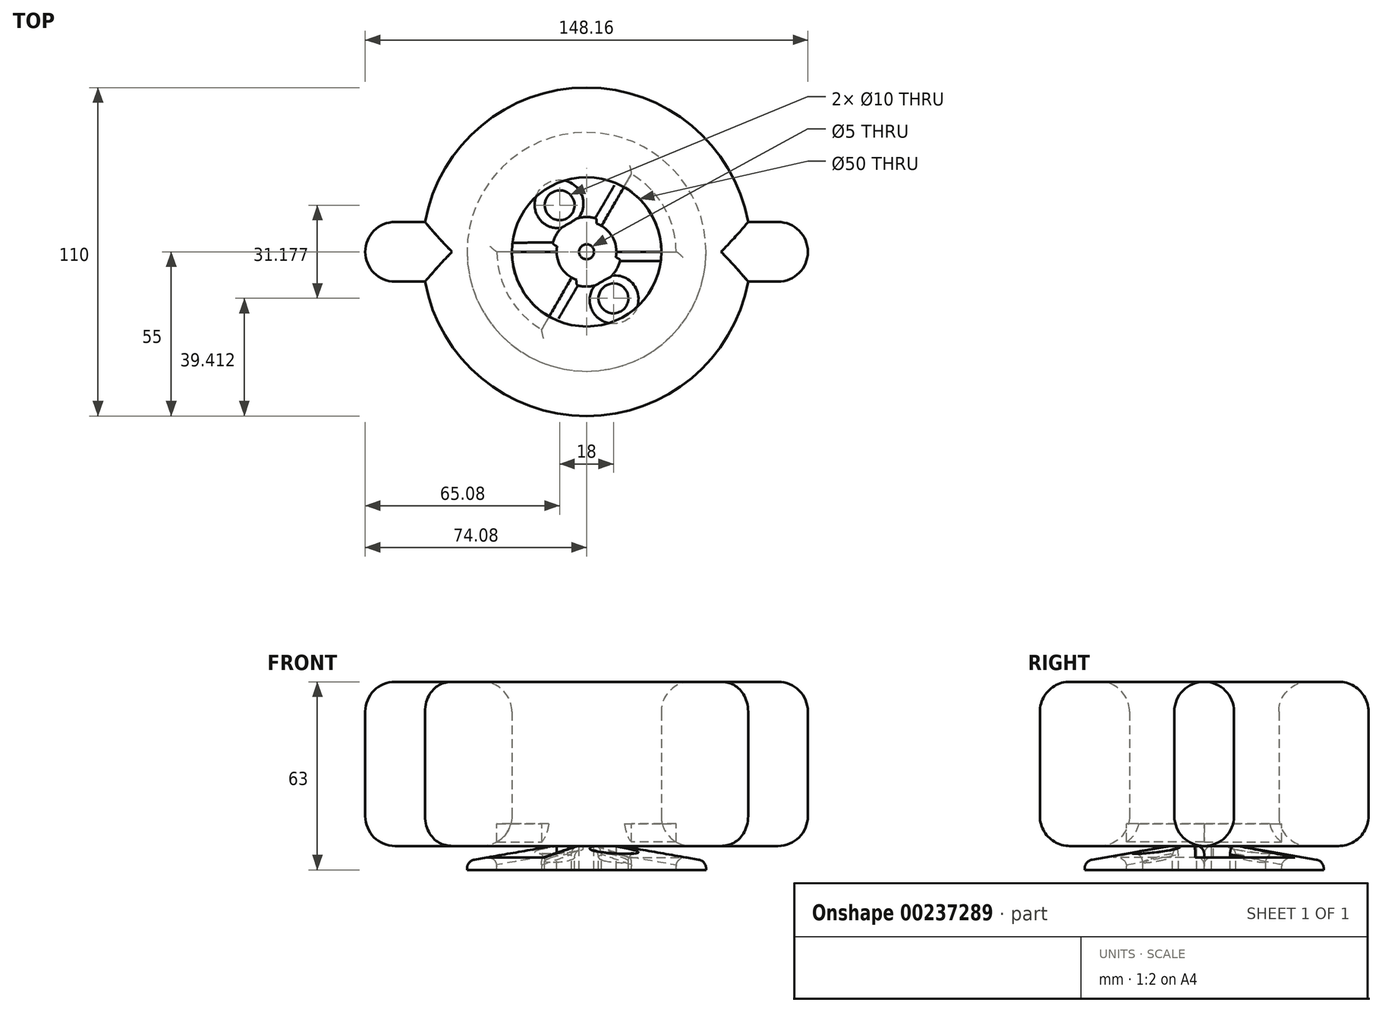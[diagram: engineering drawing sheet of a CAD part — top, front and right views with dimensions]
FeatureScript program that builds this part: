
annotation { "Feature Type Name" : "Feature", "Feature Type Description" : "" }
export const myFeature = defineFeature(function(context is Context, id is Id, definition is map)
    precondition{}
    {
        {
            var Q0;
            Q0=qCreatedBy(makeId("Top.planeOp"),FACE);
            var sketch = newSketch(context, id + "F0", { "sketchPlane" : qUnion([Q0])});
            skCircle(sketch, "E0", {"center": v(0, 0) * mm, "radius": 55 * mm});
            skCircle(sketch, "E1", {"center": v(0, 0) * mm, "radius": 25 * mm});
            skLineSegment(sketch, "E2", {"start": v(-54.08, 10) * mm, "end": v(-74.08, 10) * mm});
            skLineSegment(sketch, "E3", {"start": v(-74.08, 10) * mm, "end": v(-74.08, -10) * mm});
            skLineSegment(sketch, "E4", {"start": v(-74.08, -10) * mm, "end": v(-54.08, -10) * mm});
            skLineSegment(sketch, "E5", {"start": v(54.08, 10) * mm, "end": v(74.08, 10) * mm});
            skLineSegment(sketch, "E6", {"start": v(74.08, 10) * mm, "end": v(74.08, -10) * mm});
            skLineSegment(sketch, "E7", {"start": v(74.08, -10) * mm, "end": v(54.08, -10) * mm});
            skSolve(sketch);
        }
        {
            var Q0;
            Q0=makeQuery(id+"F0.imprint","IMPRINT",FACE,{"disambiguationData":[TD([[makeQuery(id+"F0.imprint","IMPRINT",EDGE,{"derivedFrom":sQuery(id+"F0.wireOp",EDGE,"E1")}),-1.0]])]});
            var Q1;
            {var subQ0=sQuery(id+"F0.wireOp",EDGE,"E5");Q1=makeQuery(id+"F0.imprint","IMPRINT",FACE,{"disambiguationData":[TD([[makeQuery(id+"F0.imprint","IMPRINT",EDGE,{"derivedFrom":subQ0}),-1.0]])]});}
            var Q2;
            {var subQ0=sQuery(id+"F0.wireOp",EDGE,"E2");Q2=makeQuery(id+"F0.imprint","IMPRINT",FACE,{"disambiguationData":[TD([[makeQuery(id+"F0.imprint","IMPRINT",EDGE,{"derivedFrom":subQ0}),1.0]])]});}
            extrude(context, id + "F1", {"entities" : qUnion([Q0, Q1, Q2]), "depth" : 55 * mm, "offsetDistance" : 25 * mm});
        }
        {
            var Q0;
            Q0=makeQuery(id+"F1.opExtrude","CAP_FACE",FACE,{"disambiguationData":[OSD([sQuery(id+"F0.wireOp",EDGE,"E0"),sQuery(id+"F0.wireOp",EDGE,"E1"),sQuery(id+"F0.wireOp",EDGE,"E2"),sQuery(id+"F0.wireOp",EDGE,"E3"),sQuery(id+"F0.wireOp",EDGE,"E4"),sQuery(id+"F0.wireOp",EDGE,"E5"),sQuery(id+"F0.wireOp",EDGE,"E6"),sQuery(id+"F0.wireOp",EDGE,"E7")])],"isStart":false});
            var Q1;
            Q1=makeQuery(id+"F1.opExtrude","CAP_FACE",FACE,{"disambiguationData":[OSD([sQuery(id+"F0.wireOp",EDGE,"E0"),sQuery(id+"F0.wireOp",EDGE,"E1"),sQuery(id+"F0.wireOp",EDGE,"E2"),sQuery(id+"F0.wireOp",EDGE,"E3"),sQuery(id+"F0.wireOp",EDGE,"E4"),sQuery(id+"F0.wireOp",EDGE,"E5"),sQuery(id+"F0.wireOp",EDGE,"E6"),sQuery(id+"F0.wireOp",EDGE,"E7")])],"isStart":true});
            var Q2;
            Q2=makeQuery(id+"F1.opExtrude","SWEPT_FACE",FACE,{"disambiguationData":[OSD([sQuery(id+"F0.wireOp",EDGE,"E3")])]});
            var Q3;
            Q3=makeQuery(id+"F1.opExtrude","SWEPT_FACE",FACE,{"disambiguationData":[OSD([sQuery(id+"F0.wireOp",EDGE,"E6")])]});
            fillet(context, id + "F2", {"entities" : qUnion([Q0, Q1, Q2, Q3]), "radius" : 10 * mm, "tangentPropagation" : true, "allowEdgeOverflow" : false});
        }
        {
            var Q0;
            Q0=qCreatedBy(makeId("Top.planeOp"),FACE);
            cPlane(context, id + "F3", {"entities" : qUnion([Q0]), "cplaneType" : CPlaneType.OFFSET, "offset" : 5 * mm, "oppositeDirection" : true, "width" : 150 * mm, "height" : 150 * mm});
        }
        {
            var Q0;
            Q0=qCreatedBy(id+"F3.planeOp",FACE);
            var sketch = newSketch(context, id + "F4", { "sketchPlane" : qUnion([Q0])});
            skCircle(sketch, "E8", {"center": v(0, 0) * mm, "radius": 40 * mm});
            skCircle(sketch, "E9", {"center": v(0, 0) * mm, "radius": 30 * mm});
            skCircle(sketch, "E10", {"center": v(0, 0) * mm, "radius": 10 * mm});
            skCircle(sketch, "E11", {"center": v(0, 0) * mm, "radius": 2.5 * mm});
            skLineSegment(sketch, "E12", {"start": v(10, 0) * mm, "end": v(30, 0) * mm});
            skLineSegment(sketch, "E13", {"start": v(0, 0) * mm, "end": v(15, 25.98) * mm});
            skLineSegment(sketch, "E14", {"start": v(0, 0) * mm, "end": v(-15, -25.98) * mm});
            skLineSegment(sketch, "E15", {"start": v(10, 0) * mm, "end": v(-30, 0) * mm});
            skCircle(sketch, "E16", {"center": v(9, -15.59) * mm, "radius": 5 * mm});
            skLineSegment(sketch, "E17", {"start": v(-15, -25.98) * mm, "end": v(30, 0) * mm, "construction": true});
            skLineSegment(sketch, "E18", {"start": v(-11.78, -27.59) * mm, "end": v(29.78, -3.59) * mm, "construction": true});
            skCircle(sketch, "E19.1.0", {"center": v(-9, 15.59) * mm, "radius": 5 * mm});
            skSolve(sketch);
        }
        {
            var Q0;
            {var subQ3=sQuery(id+"F4.wireOp",EDGE,"3556ffb3-3399-4bb4-9b4c-37cd51f6e398.1.0");Q0=makeQuery(id+"F4.imprint","IMPRINT",FACE,{"disambiguationData":[TD([[makeQuery(id+"F4.imprint","IMPRINT",EDGE,{"derivedFrom":subQ3}),-1.0]])]});}
            var Q1;
            {var subQ3=sQuery(id+"F4.wireOp",EDGE,"3556ffb3-3399-4bb4-9b4c-37cd51f6e398.2.0");Q1=makeQuery(id+"F4.imprint","IMPRINT",FACE,{"disambiguationData":[TD([[makeQuery(id+"F4.imprint","IMPRINT",EDGE,{"derivedFrom":subQ3}),-1.0]])]});}
            var Q2;
            {var subQ3=sQuery(id+"F4.wireOp",EDGE,"3556ffb3-3399-4bb4-9b4c-37cd51f6e398.3.0");Q2=makeQuery(id+"F4.imprint","IMPRINT",FACE,{"disambiguationData":[TD([[makeQuery(id+"F4.imprint","IMPRINT",EDGE,{"derivedFrom":subQ3}),-1.0]])]});}
            var Q3;
            {var subQ0=sQuery(id+"F4.wireOp",EDGE,"E12");Q3=makeQuery(id+"F4.imprint","IMPRINT",FACE,{"disambiguationData":[TD([[makeQuery(id+"F4.imprint","IMPRINT",EDGE,{"derivedFrom":subQ0}),-1.0]])]});}
            var Q4;
            Q4=makeQuery(id+"F4.imprint","IMPRINT",FACE,{"disambiguationData":[TD([[makeQuery(id+"F4.imprint","IMPRINT",EDGE,{"derivedFrom":sQuery(id+"F4.wireOp",EDGE,"E8")}),1.0]])]});
            var Q5;
            {var subQ1=sQuery(id+"F4.wireOp",EDGE,"E10");var subQ7=makeQuery(id+"F4.imprint","INTERSECT",VERTEX,{"derivedFrom":[subQ1,sQuery(id+"F4.wireOp",EDGE,"E12")]});Q5=makeQuery(id+"F4.imprint","IMPRINT",FACE,{"disambiguationData":[TD([[makeQuery(id+"F4.imprint","IMPRINT",EDGE,{"disambiguationData":[TD([[subQ7,-1.0]])],"derivedFrom":subQ1}),1.0]])]});}
            var Q6;
            {var subQ1=sQuery(id+"F4.wireOp",EDGE,"E10");var subQ5=makeQuery(id+"F4.imprint","INTERSECT",VERTEX,{"derivedFrom":[subQ1,sQuery(id+"F4.wireOp",EDGE,"3556ffb3-3399-4bb4-9b4c-37cd51f6e398.3.0")]});Q6=makeQuery(id+"F4.imprint","IMPRINT",FACE,{"disambiguationData":[TD([[makeQuery(id+"F4.imprint","IMPRINT",EDGE,{"disambiguationData":[TD([[subQ5,1.0]])],"derivedFrom":subQ1}),1.0]])]});}
            var Q7;
            {var subQ5=sQuery(id+"F4.wireOp",EDGE,"E10");var subQ6=makeQuery(id+"F4.imprint","INTERSECT",VERTEX,{"derivedFrom":[subQ5,sQuery(id+"F4.wireOp",EDGE,"3556ffb3-3399-4bb4-9b4c-37cd51f6e398.2.0")]});Q7=makeQuery(id+"F4.imprint","IMPRINT",FACE,{"disambiguationData":[TD([[makeQuery(id+"F4.imprint","IMPRINT",EDGE,{"disambiguationData":[TD([[subQ6,1.0]])],"derivedFrom":subQ5}),1.0]])]});}
            var Q8;
            {var subQ1=sQuery(id+"F4.wireOp",EDGE,"E10");var subQ7=makeQuery(id+"F4.imprint","INTERSECT",VERTEX,{"derivedFrom":[subQ1,sQuery(id+"F4.wireOp",EDGE,"3556ffb3-3399-4bb4-9b4c-37cd51f6e398.1.0")]});Q8=makeQuery(id+"F4.imprint","IMPRINT",FACE,{"disambiguationData":[TD([[makeQuery(id+"F4.imprint","IMPRINT",EDGE,{"disambiguationData":[TD([[subQ7,1.0]])],"derivedFrom":subQ1}),1.0]])]});}
            var Q9;
            {var subQ0=sQuery(id+"F4.wireOp",EDGE,"3556ffb3-3399-4bb4-9b4c-37cd51f6e398.2.0");Q9=makeQuery(id+"F4.imprint","IMPRINT",FACE,{"disambiguationData":[TD([[makeQuery(id+"F4.imprint","IMPRINT",EDGE,{"derivedFrom":subQ0}),1.0]])]});}
            var Q10;
            {var subQ0=sQuery(id+"F4.wireOp",EDGE,"E12");Q10=makeQuery(id+"F4.imprint","IMPRINT",FACE,{"disambiguationData":[TD([[makeQuery(id+"F4.imprint","IMPRINT",EDGE,{"derivedFrom":subQ0}),1.0]])]});}
            var Q11;
            {var subQ0=sQuery(id+"F4.wireOp",EDGE,"3556ffb3-3399-4bb4-9b4c-37cd51f6e398.3.0");Q11=makeQuery(id+"F4.imprint","IMPRINT",FACE,{"disambiguationData":[TD([[makeQuery(id+"F4.imprint","IMPRINT",EDGE,{"derivedFrom":subQ0}),1.0]])]});}
            var Q12;
            {var subQ0=sQuery(id+"F4.wireOp",EDGE,"3556ffb3-3399-4bb4-9b4c-37cd51f6e398.1.0");Q12=makeQuery(id+"F4.imprint","IMPRINT",FACE,{"disambiguationData":[TD([[makeQuery(id+"F4.imprint","IMPRINT",EDGE,{"derivedFrom":subQ0}),1.0]])]});}
            var Q13;
            {var subQ0=sQuery(id+"F4.wireOp",EDGE,"E13");var subQ1=sQuery(id+"F4.wireOp",EDGE,"E9");var subQ2=makeQuery(id+"F4.imprint","INTERSECT",VERTEX,{"derivedFrom":[subQ1,subQ0]});Q13=makeQuery(id+"F4.imprint","IMPRINT",FACE,{"disambiguationData":[TD([[makeQuery(id+"F4.imprint","IMPRINT",EDGE,{"disambiguationData":[TD([[subQ2,-1.0]])],"derivedFrom":subQ1}),1.0]])]});}
            var Q14;
            {var subQ0=sQuery(id+"F4.wireOp",EDGE,"E14");var subQ1=sQuery(id+"F4.wireOp",EDGE,"E9");var subQ2=makeQuery(id+"F4.imprint","INTERSECT",VERTEX,{"derivedFrom":[subQ1,subQ0]});Q14=makeQuery(id+"F4.imprint","IMPRINT",FACE,{"disambiguationData":[TD([[makeQuery(id+"F4.imprint","IMPRINT",EDGE,{"disambiguationData":[TD([[subQ2,1.0]])],"derivedFrom":subQ1}),1.0]])]});}
            var Q15;
            {var subQ0=sQuery(id+"F4.wireOp",EDGE,"E15");var subQ5=sQuery(id+"F4.wireOp",EDGE,"E11");var subQ7=makeQuery(id+"F4.imprint","INTERSECT",VERTEX,{"disambiguationData":[OD(0.0)],"derivedFrom":[subQ5,subQ0]});Q15=makeQuery(id+"F4.imprint","IMPRINT",FACE,{"disambiguationData":[TD([[makeQuery(id+"F4.imprint","IMPRINT",EDGE,{"disambiguationData":[TD([[subQ7,1.0]])],"derivedFrom":subQ5}),-1.0]])]});}
            var Q16;
            {var subQ0=sQuery(id+"F4.wireOp",EDGE,"E15");var subQ1=sQuery(id+"F4.wireOp",EDGE,"E11");var subQ2=makeQuery(id+"F4.imprint","INTERSECT",VERTEX,{"disambiguationData":[OD(0.0)],"derivedFrom":[subQ1,subQ0]});Q16=makeQuery(id+"F4.imprint","IMPRINT",FACE,{"disambiguationData":[TD([[makeQuery(id+"F4.imprint","IMPRINT",EDGE,{"disambiguationData":[TD([[subQ2,1.0]])],"derivedFrom":subQ1}),1.0]])]});}
            var Q17;
            {var subQ0=sQuery(id+"F4.wireOp",EDGE,"E13");var subQ1=sQuery(id+"F4.wireOp",EDGE,"E11");var subQ2=makeQuery(id+"F4.imprint","INTERSECT",VERTEX,{"derivedFrom":[subQ1,subQ0]});Q17=makeQuery(id+"F4.imprint","IMPRINT",FACE,{"disambiguationData":[TD([[makeQuery(id+"F4.imprint","IMPRINT",EDGE,{"disambiguationData":[TD([[subQ2,-1.0]])],"derivedFrom":subQ1}),1.0]])]});}
            var Q18;
            {var subQ0=sQuery(id+"F4.wireOp",EDGE,"E13");var subQ1=sQuery(id+"F4.wireOp",EDGE,"E11");var subQ2=makeQuery(id+"F4.imprint","INTERSECT",VERTEX,{"derivedFrom":[subQ1,subQ0]});Q18=makeQuery(id+"F4.imprint","IMPRINT",FACE,{"disambiguationData":[TD([[makeQuery(id+"F4.imprint","IMPRINT",EDGE,{"disambiguationData":[TD([[subQ2,1.0]])],"derivedFrom":subQ1}),1.0]])]});}
            var Q19;
            {var subQ0=sQuery(id+"F4.wireOp",EDGE,"E15");var subQ1=sQuery(id+"F4.wireOp",EDGE,"E11");var subQ2=makeQuery(id+"F4.imprint","INTERSECT",VERTEX,{"disambiguationData":[OD(1.0)],"derivedFrom":[subQ1,subQ0]});Q19=makeQuery(id+"F4.imprint","IMPRINT",FACE,{"disambiguationData":[TD([[makeQuery(id+"F4.imprint","IMPRINT",EDGE,{"disambiguationData":[TD([[subQ2,-1.0]])],"derivedFrom":subQ1}),1.0]])]});}
            var Q20;
            Q20=makeQuery(id+"F4.imprint","IMPRINT",FACE,{"disambiguationData":[TD([[makeQuery(id+"F4.imprint","IMPRINT",EDGE,{"derivedFrom":sQuery(id+"F4.wireOp",EDGE,"E19.1.0")}),1.0]])]});
            var Q21;
            Q21=makeQuery(id+"F4.imprint","IMPRINT",FACE,{"disambiguationData":[TD([[makeQuery(id+"F4.imprint","IMPRINT",EDGE,{"derivedFrom":sQuery(id+"F4.wireOp",EDGE,"E16")}),1.0]])]});
            extrude(context, id + "F5", {"entities" : qUnion([Q0, Q1, Q2, Q3, Q4, Q5, Q6, Q7, Q8, Q9, Q10, Q11, Q12, Q13, Q14, Q15, Q16, Q17, Q18, Q19, Q20, Q21]), "oppositeDirection" : true, "depth" : 3 * mm, "offsetDistance" : 25 * mm});
        }
        {
            var Q0;
            {var subQ0=sQuery(id+"F4.wireOp",EDGE,"E13");var subQ1=sQuery(id+"F4.wireOp",EDGE,"E10");var subQ2=makeQuery(id+"F4.imprint","INTERSECT",VERTEX,{"derivedFrom":[subQ1,subQ0]});Q0=makeQuery(id+"F4.imprint","IMPRINT",FACE,{"disambiguationData":[TD([[makeQuery(id+"F4.imprint","IMPRINT",EDGE,{"disambiguationData":[TD([[subQ2,-1.0]])],"derivedFrom":subQ1}),1.0]])]});}
            var Q1;
            {var subQ0=sQuery(id+"F4.wireOp",EDGE,"E15");var subQ1=sQuery(id+"F4.wireOp",EDGE,"E10");var subQ2=makeQuery(id+"F4.imprint","INTERSECT",VERTEX,{"derivedFrom":[subQ1,subQ0]});Q1=makeQuery(id+"F4.imprint","IMPRINT",FACE,{"disambiguationData":[TD([[makeQuery(id+"F4.imprint","IMPRINT",EDGE,{"disambiguationData":[TD([[subQ2,-1.0]])],"derivedFrom":subQ1}),1.0]])]});}
            var Q2;
            Q2=makeQuery(id+"F4.imprint","IMPRINT",FACE,{"disambiguationData":[TD([[makeQuery(id+"F4.imprint","IMPRINT",EDGE,{"derivedFrom":sQuery(id+"F4.wireOp",EDGE,"E8")}),1.0]])]});
            var Q3;
            {var subQ0=sQuery(id+"F4.wireOp",EDGE,"E12");Q3=makeQuery(id+"F4.imprint","IMPRINT",FACE,{"disambiguationData":[TD([[makeQuery(id+"F4.imprint","IMPRINT",EDGE,{"derivedFrom":subQ0}),-1.0]])]});}
            var Q4;
            {var subQ0=sQuery(id+"F4.wireOp",EDGE,"E13");var subQ1=sQuery(id+"F4.wireOp",EDGE,"E11");var subQ2=makeQuery(id+"F4.imprint","INTERSECT",VERTEX,{"derivedFrom":[subQ1,subQ0]});Q4=makeQuery(id+"F4.imprint","IMPRINT",FACE,{"disambiguationData":[TD([[makeQuery(id+"F4.imprint","IMPRINT",EDGE,{"disambiguationData":[TD([[subQ2,1.0]])],"derivedFrom":subQ1}),1.0]])]});}
            var Q5;
            {var subQ0=sQuery(id+"F4.wireOp",EDGE,"E13");var subQ1=sQuery(id+"F4.wireOp",EDGE,"E11");var subQ2=makeQuery(id+"F4.imprint","INTERSECT",VERTEX,{"derivedFrom":[subQ1,subQ0]});Q5=makeQuery(id+"F4.imprint","IMPRINT",FACE,{"disambiguationData":[TD([[makeQuery(id+"F4.imprint","IMPRINT",EDGE,{"disambiguationData":[TD([[subQ2,-1.0]])],"derivedFrom":subQ1}),1.0]])]});}
            var Q6;
            {var subQ0=sQuery(id+"F4.wireOp",EDGE,"E15");var subQ1=sQuery(id+"F4.wireOp",EDGE,"E11");var subQ2=makeQuery(id+"F4.imprint","INTERSECT",VERTEX,{"disambiguationData":[OD(1.0)],"derivedFrom":[subQ1,subQ0]});Q6=makeQuery(id+"F4.imprint","IMPRINT",FACE,{"disambiguationData":[TD([[makeQuery(id+"F4.imprint","IMPRINT",EDGE,{"disambiguationData":[TD([[subQ2,-1.0]])],"derivedFrom":subQ1}),1.0]])]});}
            var Q7;
            {var subQ0=sQuery(id+"F4.wireOp",EDGE,"E15");var subQ1=sQuery(id+"F4.wireOp",EDGE,"E11");var subQ2=makeQuery(id+"F4.imprint","INTERSECT",VERTEX,{"disambiguationData":[OD(0.0)],"derivedFrom":[subQ1,subQ0]});Q7=makeQuery(id+"F4.imprint","IMPRINT",FACE,{"disambiguationData":[TD([[makeQuery(id+"F4.imprint","IMPRINT",EDGE,{"disambiguationData":[TD([[subQ2,1.0]])],"derivedFrom":subQ1}),1.0]])]});}
            var Q8;
            {var subQ0=sQuery(id+"F4.wireOp",EDGE,"E13");var subQ1=sQuery(id+"F4.wireOp",EDGE,"E9");var subQ2=makeQuery(id+"F4.imprint","INTERSECT",VERTEX,{"derivedFrom":[subQ1,subQ0]});Q8=makeQuery(id+"F4.imprint","IMPRINT",FACE,{"disambiguationData":[TD([[makeQuery(id+"F4.imprint","IMPRINT",EDGE,{"disambiguationData":[TD([[subQ2,-1.0]])],"derivedFrom":subQ1}),1.0]])]});}
            var Q9;
            {var subQ0=sQuery(id+"F4.wireOp",EDGE,"E15");var subQ5=sQuery(id+"F4.wireOp",EDGE,"E11");var subQ7=makeQuery(id+"F4.imprint","INTERSECT",VERTEX,{"disambiguationData":[OD(0.0)],"derivedFrom":[subQ5,subQ0]});Q9=makeQuery(id+"F4.imprint","IMPRINT",FACE,{"disambiguationData":[TD([[makeQuery(id+"F4.imprint","IMPRINT",EDGE,{"disambiguationData":[TD([[subQ7,1.0]])],"derivedFrom":subQ5}),-1.0]])]});}
            var Q10;
            {var subQ3=sQuery(id+"F4.wireOp",EDGE,"E13");var subQ5=sQuery(id+"F4.wireOp",EDGE,"E11");var subQ6=makeQuery(id+"F4.imprint","INTERSECT",VERTEX,{"derivedFrom":[subQ5,subQ3]});Q10=makeQuery(id+"F4.imprint","IMPRINT",FACE,{"disambiguationData":[TD([[makeQuery(id+"F4.imprint","IMPRINT",EDGE,{"disambiguationData":[TD([[subQ6,1.0]])],"derivedFrom":subQ5}),-1.0]])]});}
            var Q11;
            {var subQ0=sQuery(id+"F4.wireOp",EDGE,"E12");Q11=makeQuery(id+"F4.imprint","IMPRINT",FACE,{"disambiguationData":[TD([[makeQuery(id+"F4.imprint","IMPRINT",EDGE,{"derivedFrom":subQ0}),1.0]])]});}
            var Q12;
            {var subQ0=sQuery(id+"F4.wireOp",EDGE,"E14");var subQ1=sQuery(id+"F4.wireOp",EDGE,"E9");var subQ2=makeQuery(id+"F4.imprint","INTERSECT",VERTEX,{"derivedFrom":[subQ1,subQ0]});Q12=makeQuery(id+"F4.imprint","IMPRINT",FACE,{"disambiguationData":[TD([[makeQuery(id+"F4.imprint","IMPRINT",EDGE,{"disambiguationData":[TD([[subQ2,1.0]])],"derivedFrom":subQ1}),1.0]])]});}
            var Q13;
            Q13=makeQuery(id+"F4.imprint","IMPRINT",FACE,{"disambiguationData":[TD([[makeQuery(id+"F4.imprint","IMPRINT",EDGE,{"derivedFrom":sQuery(id+"F4.wireOp",EDGE,"E19.1.0")}),1.0]])]});
            var Q14;
            Q14=makeQuery(id+"F4.imprint","IMPRINT",FACE,{"disambiguationData":[TD([[makeQuery(id+"F4.imprint","IMPRINT",EDGE,{"derivedFrom":sQuery(id+"F4.wireOp",EDGE,"E16")}),1.0]])]});
            extrude(context, id + "F6", {"entities" : qUnion([Q0, Q1, Q2, Q3, Q4, Q5, Q6, Q7, Q8, Q9, Q10, Q11, Q12, Q13, Q14]), "operationType" : NewBodyOperationType.ADD, "depth" : 5 * mm, "offsetDistance" : 25 * mm, "hasDraft" : true, "draftAngle" : 80 * degree, "draftPullDirection" : true});
        }
        {
            var Q0;
            {var subQ0=sQuery(id+"F4.wireOp",EDGE,"E14");var subQ1=sQuery(id+"F4.wireOp",EDGE,"E9");var subQ2=makeQuery(id+"F4.imprint","INTERSECT",VERTEX,{"derivedFrom":[subQ1,subQ0]});Q0=makeQuery(id+"F4.imprint","IMPRINT",FACE,{"disambiguationData":[TD([[makeQuery(id+"F4.imprint","IMPRINT",EDGE,{"disambiguationData":[TD([[subQ2,1.0]])],"derivedFrom":subQ1}),1.0]])]});}
            var Q1;
            {var subQ0=sQuery(id+"F4.wireOp",EDGE,"E15");var subQ1=sQuery(id+"F4.wireOp",EDGE,"E11");var subQ2=makeQuery(id+"F4.imprint","INTERSECT",VERTEX,{"disambiguationData":[OD(0.0)],"derivedFrom":[subQ1,subQ0]});Q1=makeQuery(id+"F4.imprint","IMPRINT",FACE,{"disambiguationData":[TD([[makeQuery(id+"F4.imprint","IMPRINT",EDGE,{"disambiguationData":[TD([[subQ2,1.0]])],"derivedFrom":subQ1}),1.0]])]});}
            var Q2;
            {var subQ0=sQuery(id+"F4.wireOp",EDGE,"E13");var subQ1=sQuery(id+"F4.wireOp",EDGE,"E11");var subQ2=makeQuery(id+"F4.imprint","INTERSECT",VERTEX,{"derivedFrom":[subQ1,subQ0]});Q2=makeQuery(id+"F4.imprint","IMPRINT",FACE,{"disambiguationData":[TD([[makeQuery(id+"F4.imprint","IMPRINT",EDGE,{"disambiguationData":[TD([[subQ2,-1.0]])],"derivedFrom":subQ1}),1.0]])]});}
            var Q3;
            {var subQ0=sQuery(id+"F4.wireOp",EDGE,"E13");var subQ1=sQuery(id+"F4.wireOp",EDGE,"E11");var subQ2=makeQuery(id+"F4.imprint","INTERSECT",VERTEX,{"derivedFrom":[subQ1,subQ0]});Q3=makeQuery(id+"F4.imprint","IMPRINT",FACE,{"disambiguationData":[TD([[makeQuery(id+"F4.imprint","IMPRINT",EDGE,{"disambiguationData":[TD([[subQ2,1.0]])],"derivedFrom":subQ1}),1.0]])]});}
            var Q4;
            {var subQ0=sQuery(id+"F4.wireOp",EDGE,"E15");var subQ1=sQuery(id+"F4.wireOp",EDGE,"E11");var subQ2=makeQuery(id+"F4.imprint","INTERSECT",VERTEX,{"disambiguationData":[OD(1.0)],"derivedFrom":[subQ1,subQ0]});Q4=makeQuery(id+"F4.imprint","IMPRINT",FACE,{"disambiguationData":[TD([[makeQuery(id+"F4.imprint","IMPRINT",EDGE,{"disambiguationData":[TD([[subQ2,-1.0]])],"derivedFrom":subQ1}),1.0]])]});}
            var Q5;
            {var subQ0=sQuery(id+"F4.wireOp",EDGE,"E12");Q5=makeQuery(id+"F4.imprint","IMPRINT",FACE,{"disambiguationData":[TD([[makeQuery(id+"F4.imprint","IMPRINT",EDGE,{"derivedFrom":subQ0}),1.0]])]});}
            var Q6;
            Q6=makeQuery(id+"F4.imprint","IMPRINT",FACE,{"disambiguationData":[TD([[makeQuery(id+"F4.imprint","IMPRINT",EDGE,{"derivedFrom":sQuery(id+"F4.wireOp",EDGE,"E19.1.0")}),1.0]])]});
            var Q7;
            Q7=makeQuery(id+"F4.imprint","IMPRINT",FACE,{"disambiguationData":[TD([[makeQuery(id+"F4.imprint","IMPRINT",EDGE,{"derivedFrom":sQuery(id+"F4.wireOp",EDGE,"E16")}),1.0]])]});
            extrude(context, id + "F7", {"entities" : qUnion([Q0, Q1, Q2, Q3, Q4, Q5, Q6, Q7]), "operationType" : NewBodyOperationType.REMOVE, "oppositeDirection" : true, "depth" : 25 * mm, "offsetDistance" : 25 * mm, "symmetric" : true});
        }
        {
            var Q0;
            Q0=makeQuery(id+"F7.boolean.opBoolean","INTERSECT",EDGE,{"derivedFrom":[makeQuery(id+"F6.opExtrude","SWEPT_FACE",FACE,{"disambiguationData":[OSD([sQuery(id+"F4.wireOp",EDGE,"E8")])]}),makeQuery(id+"F7.opExtrude","SWEPT_FACE",FACE,{"disambiguationData":[OSD([sQuery(id+"F4.wireOp",EDGE,"E19.1.0")])]})]});
            var Q1;
            Q1=makeQuery(id+"F7.boolean.opBoolean","INTERSECT",EDGE,{"derivedFrom":[makeQuery(id+"F6.opExtrude","SWEPT_FACE",FACE,{"disambiguationData":[OSD([sQuery(id+"F4.wireOp",EDGE,"E8")])]}),makeQuery(id+"F7.opExtrude","SWEPT_FACE",FACE,{"disambiguationData":[OSD([sQuery(id+"F4.wireOp",EDGE,"E16")])]})]});
            var Q2;
            Q2=makeQuery(id+"F7.boolean.opBoolean","INTERSECT",EDGE,{"derivedFrom":[makeQuery(id+"F6.opExtrude","SWEPT_FACE",FACE,{"disambiguationData":[OSD([sQuery(id+"F4.wireOp",EDGE,"E8")])]}),makeQuery(id+"F7.opExtrude","SWEPT_FACE",FACE,{"disambiguationData":[OSD([sQuery(id+"F4.wireOp",EDGE,"E13")])]})]});
            var Q3;
            {var subQ0=sQuery(id+"F4.wireOp",EDGE,"E9");Q3=makeQuery(id+"F7.boolean.opBoolean","INTERSECT",EDGE,{"derivedFrom":[makeQuery(id+"F6.opExtrude","SWEPT_FACE",FACE,{"disambiguationData":[OSD([sQuery(id+"F4.wireOp",EDGE,"E8")])]}),makeQuery(id+"F7.opExtrude","SWEPT_FACE",FACE,{"disambiguationData":[OSD([subQ0]),TDD([makeQuery(id+"F4.imprint","IMPRINT",EDGE,{"disambiguationData":[TD([[makeQuery(id+"F4.imprint","INTERSECT",VERTEX,{"derivedFrom":[subQ0,sQuery(id+"F4.wireOp",EDGE,"E12")]}),-1.0]])],"derivedFrom":subQ0})])]})]});}
            var Q4;
            Q4=makeQuery(id+"F7.boolean.opBoolean","INTERSECT",EDGE,{"derivedFrom":[makeQuery(id+"F6.opExtrude","SWEPT_FACE",FACE,{"disambiguationData":[OSD([sQuery(id+"F4.wireOp",EDGE,"E8")])]}),makeQuery(id+"F7.opExtrude","SWEPT_FACE",FACE,{"disambiguationData":[OSD([sQuery(id+"F4.wireOp",EDGE,"E12")])]})]});
            var Q5;
            Q5=makeQuery(id+"F7.boolean.opBoolean","INTERSECT",EDGE,{"derivedFrom":[makeQuery(id+"F6.opExtrude","SWEPT_FACE",FACE,{"disambiguationData":[OSD([sQuery(id+"F4.wireOp",EDGE,"E8")])]}),makeQuery(id+"F7.opExtrude","SWEPT_FACE",FACE,{"disambiguationData":[OSD([sQuery(id+"F4.wireOp",EDGE,"E14")])]})]});
            var Q6;
            {var subQ0=sQuery(id+"F4.wireOp",EDGE,"E9");Q6=makeQuery(id+"F7.boolean.opBoolean","INTERSECT",EDGE,{"derivedFrom":[makeQuery(id+"F6.opExtrude","SWEPT_FACE",FACE,{"disambiguationData":[OSD([sQuery(id+"F4.wireOp",EDGE,"E8")])]}),makeQuery(id+"F7.opExtrude","SWEPT_FACE",FACE,{"disambiguationData":[OSD([subQ0]),TDD([makeQuery(id+"F4.imprint","IMPRINT",EDGE,{"disambiguationData":[TD([[makeQuery(id+"F4.imprint","INTERSECT",VERTEX,{"derivedFrom":[subQ0,sQuery(id+"F4.wireOp",EDGE,"E14")]}),1.0]])],"derivedFrom":subQ0})])]})]});}
            var Q7;
            Q7=makeQuery(id+"F7.boolean.opBoolean","INTERSECT",EDGE,{"derivedFrom":[makeQuery(id+"F6.opExtrude","SWEPT_FACE",FACE,{"disambiguationData":[OSD([sQuery(id+"F4.wireOp",EDGE,"E8")])]}),makeQuery(id+"F7.opExtrude","SWEPT_FACE",FACE,{"disambiguationData":[OSD([sQuery(id+"F4.wireOp",EDGE,"E15")])]})]});
            var Q8;
            {var subQ0=sQuery(id+"F4.wireOp",EDGE,"E8");Q8=makeQuery(id+"F6.boolean.opBoolean","MERGE",EDGE,{"derivedFrom":[makeQuery(id+"F5.opExtrude","CAP_EDGE",EDGE,{"disambiguationData":[OSD([subQ0])],"isStart":true}),makeQuery(id+"F6.opExtrude","CAP_EDGE",EDGE,{"disambiguationData":[OSD([subQ0])],"isStart":true})]});}
            fillet(context, id + "F8", {"entities" : qUnion([Q0, Q1, Q2, Q3, Q4, Q5, Q6, Q7, Q8]), "radius" : 3 * mm, "tangentPropagation" : true, "allowEdgeOverflow" : false});
        }
    });
